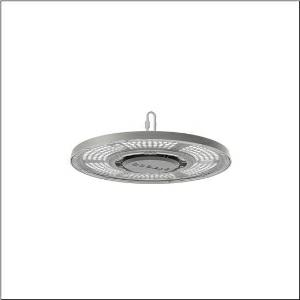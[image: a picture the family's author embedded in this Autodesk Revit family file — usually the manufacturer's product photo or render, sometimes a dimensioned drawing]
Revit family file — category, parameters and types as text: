
# Revit family: highbay_31-s_51hc42da4fmb
name_source: partatom
category: Lighting Fixtures
units: mm (PartAtom-declared; Revit-internal decimal feet)

## family parameters
Cut with Voids When Loaded = No
Host = Face
Light Source = No
Part Type = Normal
Room Calculation Point = No
Round Connector Dimension = Use Diameter
Shared = No

## types (1)
- Highbay 31-S (1 x LED, 14000 lm, 94 W, 4000K)
    Apparent Load = 94 VA
    CIE Flux Codes = 77 99 100 100 100
    Color Rendering = 80
    Color Temperature = 4000K
    Default Elevation = 1800 mm
    Description = Highbay 31-S, LED high bay luminaire, primary light control with lens, of PC, primary optical cover: cover panel, of PC, transparent, light emission: direct distribution, primary light characteristic: rotationally symmetric, installation type: suspended mounting, surface-mounted, LED, rated luminous flux: 14.000lm, luminous efficacy: 150lm/W, light colour: 840, colour temperature: 4000K, control gear: ECG DALI, with cable, 5x 1.0mm², free wire ends, mains connection: 220..240V, AC/DC, 0/50..60Hz, cable length: 1,5m, rated input power: 94W, housing, rotationally symmetric, of diecast aluminium, grey aluminium (RAL 9007), diameter: 339mm, protection rating (complete): IP65, insulation class (complete): insulation class I (protective earthing), certification: CE, ENEC, UKCA, protection symbol: D, impact resistance: IK08, permissible operating ambient temperature: -30..+45°C, standard: EN 60598-2-22, EN 60598, corresponds to IFS (International Featured Standards) requirements for safety and quality in the food industry, packaging unit: 1 piece
    Height = 141 mm
    Lamp = 1 x LED
    Lamp Light Flux = 14000 lm
    Lamp Power = 94 W
    Lamp count = 1
    Length = 339 mm
    Luminous efficacy = 149 lm/W
    Manufacturer = Siteco
    ModVariant = No
    Model = 51HC42DA4FMB
    Mounting Place = Ceiling
    Mounting Type = Pendant
    Number of Poles = 1
    OnlyDefault = Yes
    Power Factor = 1
    Product Name = Highbay 31-S
    Product group = LED high bay luminaire
    ProductGroupID = 903
    Protection Class = Protection class I
    Protection Degree = IP 65
    RLX_Detail_Level = 1
    RlxData = <blob elided: 162545 chars, md5=450bc6db>
    Socket = socket
    Standby Power = 0 W
    System Light Flux = 14000 lm
    System Power = 94 W
    Type Comments = Product without accessories
    Type Image = l_1007237.jpg
    URL = http://relux.com
    VarID = ---
    Voltage = 0 V
    Weight = 0.00 kg
    Width = 0 mm  [stored 0 ft]

note: [stored X ft] marks values corroborated as IEEE doubles in the binary element streams (Revit-internal decimal feet)

## geometry (parser evidence)
native form markers: Blend x4, Sweep x9
no freeform markers — native parametric forms only
